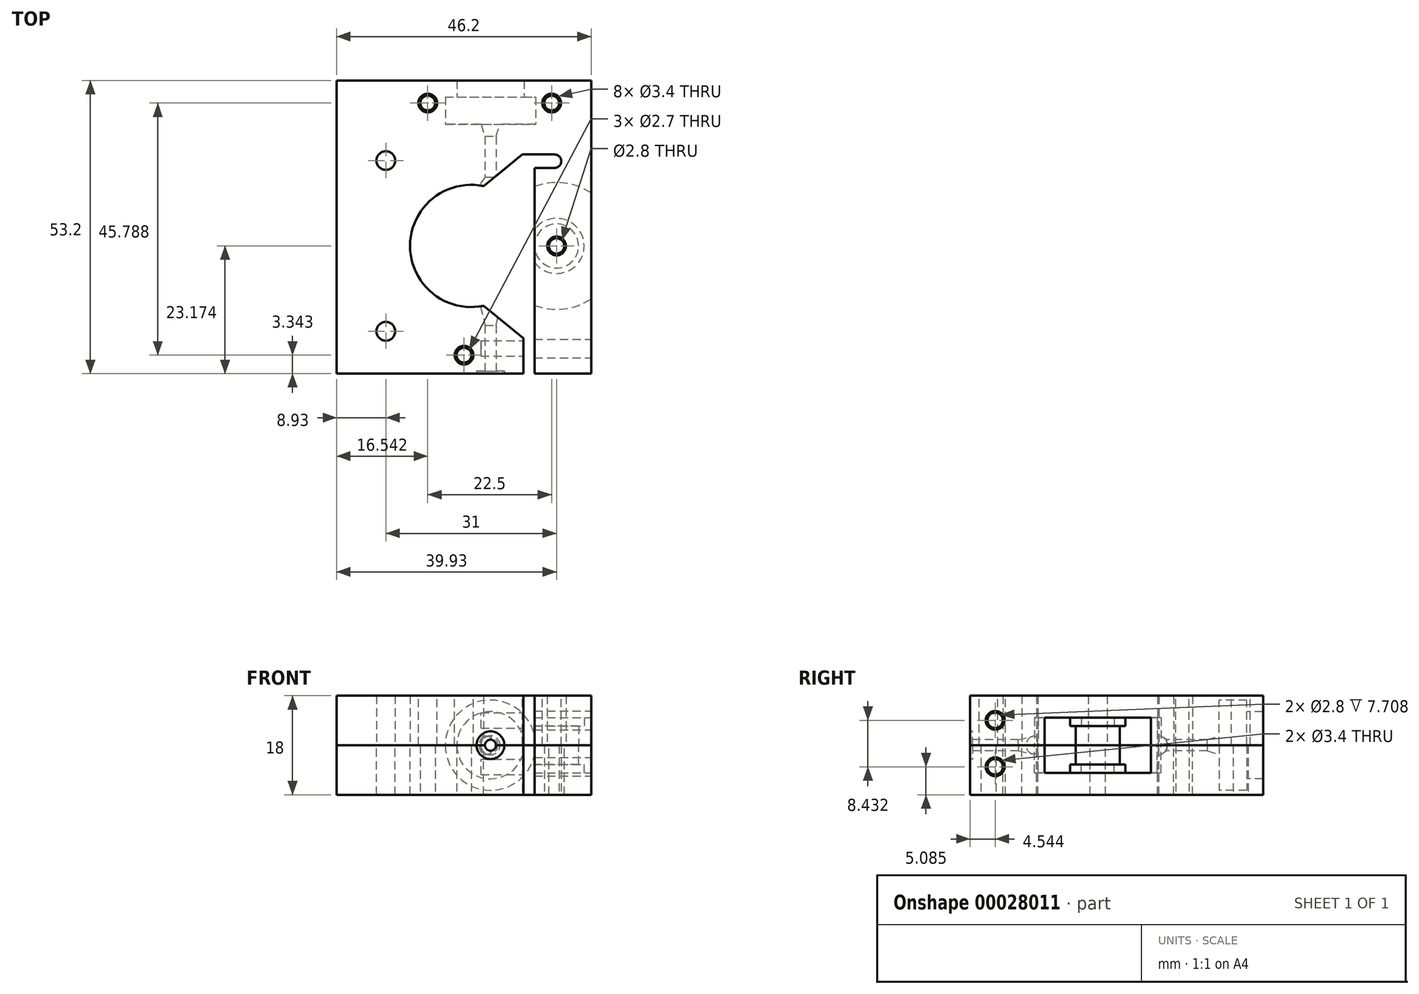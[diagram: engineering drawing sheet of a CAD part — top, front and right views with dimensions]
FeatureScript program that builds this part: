
annotation { "Feature Type Name" : "Feature", "Feature Type Description" : "" }
export const myFeature = defineFeature(function(context is Context, id is Id, definition is map)
    precondition{}
    {
        {
            var Q0;
            Q0=qCreatedBy(makeId("Top.planeOp"),FACE);
            var sketch = newSketch(context, id + "F0", { "sketchPlane" : qUnion([Q0])});
            skLineSegment(sketch, "E0", {"start": v(-24.43, 35.85) * mm, "end": v(-24.43, -17.36) * mm});
            skLineSegment(sketch, "E1", {"start": v(-24.43, -17.36) * mm, "end": v(-24.43, -17.36) * mm});
            skLineSegment(sketch, "E2", {"start": v(-24.43, -17.36) * mm, "end": v(-24.43, -17.35) * mm});
            skLineSegment(sketch, "E3", {"start": v(-24.43, -17.35) * mm, "end": v(9.48, -17.35) * mm});
            skLineSegment(sketch, "E4", {"start": v(9.48, -17.35) * mm, "end": v(9.48, 22.43) * mm});
            skLineSegment(sketch, "E5", {"start": v(9.48, 22.43) * mm, "end": v(15.14, 22.43) * mm});
            skLineSegment(sketch, "E6", {"start": v(15.14, 20) * mm, "end": v(11.48, 20) * mm});
            skLineSegment(sketch, "E7", {"start": v(11.48, 20) * mm, "end": v(11.48, -17.35) * mm});
            skLineSegment(sketch, "E8", {"start": v(11.48, -17.35) * mm, "end": v(21.77, -17.35) * mm});
            skLineSegment(sketch, "E9", {"start": v(21.77, -17.35) * mm, "end": v(21.77, 35.85) * mm});
            skLineSegment(sketch, "E10", {"start": v(21.77, 35.85) * mm, "end": v(-24.43, 35.85) * mm});
            skCircle(sketch, "E11", {"center": v(-7.89, 31.78) * mm, "radius": 1.35 * mm});
            skCircle(sketch, "E12", {"center": v(14.61, 31.78) * mm, "radius": 1.35 * mm});
            skCircle(sketch, "E13", {"center": v(-1.3, -14) * mm, "radius": 1.35 * mm});
            skArc(sketch, "E14", {"start": v(15.14, 20) * mm, "mid": v(16.35, 21.21) * mm, "end": v(15.14, 22.43) * mm});
            skCircle(sketch, "E15", {"center": v(-7.89, 31.78) * mm, "radius": 1.7 * mm});
            skCircle(sketch, "E16", {"center": v(14.61, 31.78) * mm, "radius": 1.7 * mm});
            skCircle(sketch, "E17", {"center": v(-1.3, -14) * mm, "radius": 1.7 * mm});
            skSolve(sketch);
        }
        {
            var Q0;
            Q0=makeQuery(id+"F0.imprint","IMPRINT",FACE,{"disambiguationData":[TD([[makeQuery(id+"F0.imprint","IMPRINT",EDGE,{"derivedFrom":sQuery(id+"F0.wireOp",EDGE,"E0")}),1.0]])]});
            var Q1;
            Q1=makeQuery(id+"F0.imprint","IMPRINT",FACE,{"disambiguationData":[TD([[makeQuery(id+"F0.imprint","IMPRINT",EDGE,{"derivedFrom":sQuery(id+"F0.wireOp",EDGE,"E11")}),-1.0]])]});
            var Q2;
            Q2=makeQuery(id+"F0.imprint","IMPRINT",FACE,{"disambiguationData":[TD([[makeQuery(id+"F0.imprint","IMPRINT",EDGE,{"derivedFrom":sQuery(id+"F0.wireOp",EDGE,"E12")}),-1.0]])]});
            var Q3;
            Q3=makeQuery(id+"F0.imprint","IMPRINT",FACE,{"disambiguationData":[TD([[makeQuery(id+"F0.imprint","IMPRINT",EDGE,{"derivedFrom":sQuery(id+"F0.wireOp",EDGE,"E13")}),-1.0]])]});
            extrude(context, id + "F1", {"entities" : qUnion([Q0, Q1, Q2, Q3]), "depth" : 9 * mm});
        }
        {
            var Q0;
            Q0=makeQuery(id+"F1.opExtrude","CAP_FACE",FACE,{"disambiguationData":[OSD([sQuery(id+"F0.wireOp",EDGE,"E0"),sQuery(id+"F0.wireOp",EDGE,"E1"),sQuery(id+"F0.wireOp",EDGE,"E2"),sQuery(id+"F0.wireOp",EDGE,"E3"),sQuery(id+"F0.wireOp",EDGE,"E4"),sQuery(id+"F0.wireOp",EDGE,"E5"),sQuery(id+"F0.wireOp",EDGE,"E6"),sQuery(id+"F0.wireOp",EDGE,"E7"),sQuery(id+"F0.wireOp",EDGE,"E8"),sQuery(id+"F0.wireOp",EDGE,"E9"),sQuery(id+"F0.wireOp",EDGE,"E10"),sQuery(id+"F0.wireOp",EDGE,"604cad85-587a-4b7d-8070-06f4cba85480"),sQuery(id+"F0.wireOp",EDGE,"6e5e38c1-5bff-4efe-a8c5-b84022f0a049"),sQuery(id+"F0.wireOp",EDGE,"b8144507-9dd7-4af4-87a3-7b649dd00ae6"),sQuery(id+"F0.wireOp",EDGE,"b9c2cb7c-5e58-4995-888e-a78f0403fbb5"),sQuery(id+"F0.wireOp",EDGE,"885990ab-7576-4c23-8475-595d2769e284"),sQuery(id+"F0.wireOp",EDGE,"E11"),sQuery(id+"F0.wireOp",EDGE,"E12"),sQuery(id+"F0.wireOp",EDGE,"E13"),sQuery(id+"F0.wireOp",EDGE,"E14")])],"isStart":false});
            var sketch = newSketch(context, id + "F2", { "sketchPlane" : qUnion([Q0])});
            skCircle(sketch, "E18", {"center": v(0, 5.82) * mm, "radius": 11.1 * mm});
            skCircle(sketch, "E19", {"center": v(-15.5, 21.32) * mm, "radius": 1.7 * mm});
            skCircle(sketch, "E20", {"center": v(-15.5, -9.68) * mm, "radius": 1.7 * mm});
            skSolve(sketch);
        }
        {
            var Q0;
            Q0=qSketchRegion(id+"F2",true);
            extrude(context, id + "F3", {"entities" : qUnion([Q0]), "operationType" : NewBodyOperationType.REMOVE, "endBound" : BoundingType.THROUGH_ALL, "oppositeDirection" : true, "depth" : 25 * mm});
        }
        {
            var Q0;
            Q0=makeQuery(id+"F1.opExtrude","CAP_FACE",FACE,{"disambiguationData":[OSD([sQuery(id+"F0.wireOp",EDGE,"E0"),sQuery(id+"F0.wireOp",EDGE,"E1"),sQuery(id+"F0.wireOp",EDGE,"E2"),sQuery(id+"F0.wireOp",EDGE,"E3"),sQuery(id+"F0.wireOp",EDGE,"E4"),sQuery(id+"F0.wireOp",EDGE,"E5"),sQuery(id+"F0.wireOp",EDGE,"E6"),sQuery(id+"F0.wireOp",EDGE,"E7"),sQuery(id+"F0.wireOp",EDGE,"E8"),sQuery(id+"F0.wireOp",EDGE,"E9"),sQuery(id+"F0.wireOp",EDGE,"E10"),sQuery(id+"F0.wireOp",EDGE,"604cad85-587a-4b7d-8070-06f4cba85480"),sQuery(id+"F0.wireOp",EDGE,"6e5e38c1-5bff-4efe-a8c5-b84022f0a049"),sQuery(id+"F0.wireOp",EDGE,"E11"),sQuery(id+"F0.wireOp",EDGE,"E12"),sQuery(id+"F0.wireOp",EDGE,"E13"),sQuery(id+"F0.wireOp",EDGE,"E14")])],"isStart":false});
            var sketch = newSketch(context, id + "F4", { "sketchPlane" : qUnion([Q0])});
            skCircle(sketch, "E21", {"center": v(15.5, 5.82) * mm, "radius": 11.5 * mm});
            skCircle(sketch, "E22", {"center": v(15.5, 5.82) * mm, "radius": 5 * mm});
            skCircle(sketch, "E23", {"center": v(15.5, 5.82) * mm, "radius": 4 * mm});
            skLineSegment(sketch, "E24", {"start": v(0, 5.82) * mm, "end": v(31, 5.82) * mm, "construction": true});
            skCircle(sketch, "E25", {"center": v(15.5, 5.82) * mm, "radius": 1.4 * mm});
            skCircle(sketch, "E26", {"center": v(15.5, 5.82) * mm, "radius": 1.7 * mm});
            skSolve(sketch);
        }
        {
            var Q0;
            Q0=makeQuery(id+"F4.imprint","IMPRINT",FACE,{"disambiguationData":[TD([[makeQuery(id+"F4.imprint","IMPRINT",EDGE,{"derivedFrom":sQuery(id+"F4.wireOp",EDGE,"E22")}),-1.0]])]});
            extrude(context, id + "F5", {"entities" : qUnion([Q0]), "operationType" : NewBodyOperationType.REMOVE, "oppositeDirection" : true, "depth" : 5 * mm});
        }
        {
            var Q0;
            Q0=makeQuery(id+"F4.imprint","IMPRINT",FACE,{"disambiguationData":[TD([[makeQuery(id+"F4.imprint","IMPRINT",EDGE,{"derivedFrom":sQuery(id+"F4.wireOp",EDGE,"E22")}),1.0]])]});
            var Q1;
            Q1=makeQuery(id+"F4.imprint","IMPRINT",FACE,{"disambiguationData":[TD([[makeQuery(id+"F4.imprint","IMPRINT",EDGE,{"derivedFrom":sQuery(id+"F4.wireOp",EDGE,"E23")}),-1.0]])]});
            extrude(context, id + "F6", {"entities" : qUnion([Q0, Q1]), "operationType" : NewBodyOperationType.REMOVE, "oppositeDirection" : true, "depth" : 3.5 * mm});
        }
        {
            var Q0;
            {var subQ0=sQuery(id+"F0.wireOp",EDGE,"E0");var subQ1=sQuery(id+"F0.wireOp",EDGE,"E1");var subQ2=sQuery(id+"F0.wireOp",EDGE,"E2");var subQ3=sQuery(id+"F0.wireOp",EDGE,"E3");var subQ4=sQuery(id+"F0.wireOp",EDGE,"E4");var subQ5=sQuery(id+"F0.wireOp",EDGE,"E5");var subQ6=sQuery(id+"F0.wireOp",EDGE,"E6");var subQ7=sQuery(id+"F0.wireOp",EDGE,"E7");var subQ8=sQuery(id+"F0.wireOp",EDGE,"E9");var subQ9=sQuery(id+"F0.wireOp",EDGE,"E10");var subQ10=sQuery(id+"F0.wireOp",EDGE,"604cad85-587a-4b7d-8070-06f4cba85480");var subQ11=sQuery(id+"F0.wireOp",EDGE,"6e5e38c1-5bff-4efe-a8c5-b84022f0a049");var subQ12=sQuery(id+"F0.wireOp",EDGE,"E11");var subQ13=sQuery(id+"F0.wireOp",EDGE,"E12");var subQ14=sQuery(id+"F0.wireOp",EDGE,"E13");var subQ15=sQuery(id+"F0.wireOp",EDGE,"E14");Q0=makeQuery(id+"F5.boolean.opBoolean","SPLIT",FACE,{"disambiguationData":[TD([makeQuery(id+"F1.opExtrude","SWEPT_FACE",FACE,{"disambiguationData":[OSD([subQ0])]})])],"derivedFrom":makeQuery(id+"F1.opExtrude","CAP_FACE",FACE,{"disambiguationData":[OSD([subQ0,subQ1,subQ2,subQ3,subQ4,subQ5,subQ6,subQ7,sQuery(id+"F0.wireOp",EDGE,"E8"),subQ8,subQ9,subQ10,subQ11,subQ12,subQ13,subQ14,subQ15])],"isStart":false})});}
            var sketch = newSketch(context, id + "F7", { "sketchPlane" : qUnion([Q0])});
            skLineSegment(sketch, "E27", {"start": v(3.5, 14.7) * mm, "end": v(3.5, 37.09) * mm});
            skLineSegment(sketch, "E28", {"start": v(0, 5.82) * mm, "end": v(31.4, 5.82) * mm, "construction": true});
            skLineSegment(sketch, "E29.0.MirrorCS", {"start": v(0.98, -16.94) * mm, "end": v(2.5, -16.94) * mm});
            skLineSegment(sketch, "E29.1.MirrorCS", {"start": v(3.5, -3.06) * mm, "end": v(3.5, -25.44) * mm});
            skLineSegment(sketch, "E29.2.MirrorCS", {"start": v(0.98, -25.44) * mm, "end": v(0.98, -16.94) * mm});
            skLineSegment(sketch, "E29.3.MirrorCS", {"start": v(1.31, -3.53) * mm, "end": v(3.5, -3.06) * mm});
            skLineSegment(sketch, "E29.4.MirrorCS", {"start": v(2.5, -8.56) * mm, "end": v(1.31, -3.53) * mm});
            skLineSegment(sketch, "E29.5.MirrorCS", {"start": v(2.5, -16.94) * mm, "end": v(2.5, -8.56) * mm});
            skLineSegment(sketch, "E29.6.MirrorCS", {"start": v(3.5, -25.44) * mm, "end": v(0.98, -25.44) * mm});
            skLineSegment(sketch, "E30", {"start": v(-2.6, 37.09) * mm, "end": v(-2.6, 32.89) * mm});
            skLineSegment(sketch, "E31", {"start": v(-2.6, 32.89) * mm, "end": v(-4.7, 32.89) * mm});
            skLineSegment(sketch, "E32", {"start": v(-4.7, 32.89) * mm, "end": v(-4.7, 27.89) * mm});
            skLineSegment(sketch, "E33", {"start": v(-4.7, 27.89) * mm, "end": v(1.77, 27.89) * mm});
            skLineSegment(sketch, "E34", {"start": v(1.77, 27.89) * mm, "end": v(2.5, 25.73) * mm});
            skLineSegment(sketch, "E35", {"start": v(2.5, 25.73) * mm, "end": v(2.5, 18.34) * mm});
            skLineSegment(sketch, "E36", {"start": v(-2.6, 37.09) * mm, "end": v(3.5, 37.09) * mm});
            skLineSegment(sketch, "E37", {"start": v(2.5, 18.34) * mm, "end": v(0, 14.7) * mm});
            skLineSegment(sketch, "E38", {"start": v(0, 14.7) * mm, "end": v(3.5, 14.7) * mm});
            skSolve(sketch);
        }
        {
            var Q0;
            Q0=qSketchRegion(id+"F7",true);
            var Q1;
            Q1=sQuery(id+"F7.wireOp",EDGE,"E27");
            revolve(context, id + "F8", {"entities" : qUnion([Q0]), "axis" : qUnion([Q1]), "revolveType" : RevolveType.FULL});
        }
        {
            var Q0;
            Q0=makeQuery(id+"F8.opRevolve","SWEPT_BODY",BODY,{"disambiguationData":[OSD([sQuery(id+"F7.wireOp",EDGE,"0e4a01cc-4869-4b9d-8ca2-1c94110d196d"),sQuery(id+"F7.wireOp",EDGE,"4d913e13-2244-4a79-84d2-82f6c5de00b3"),sQuery(id+"F7.wireOp",EDGE,"1203443b-fa58-4cec-9fe4-144960d3b7c2"),sQuery(id+"F7.wireOp",EDGE,"f73e5a92-9274-40af-91db-ab5fa52ec61f"),sQuery(id+"F7.wireOp",EDGE,"4cc6588a-36a6-4115-9f4e-735cf5f17870"),sQuery(id+"F7.wireOp",EDGE,"E27"),sQuery(id+"F7.wireOp",EDGE,"0bbee7b9-97e0-41c3-ac0e-625151f8027d")])]});
            var Q1;
            Q1=makeQuery(id+"F1.opExtrude","SWEPT_BODY",BODY,{"disambiguationData":[OSD([sQuery(id+"F0.wireOp",EDGE,"E0"),sQuery(id+"F0.wireOp",EDGE,"E1"),sQuery(id+"F0.wireOp",EDGE,"E2"),sQuery(id+"F0.wireOp",EDGE,"E3"),sQuery(id+"F0.wireOp",EDGE,"E4"),sQuery(id+"F0.wireOp",EDGE,"E5"),sQuery(id+"F0.wireOp",EDGE,"E6"),sQuery(id+"F0.wireOp",EDGE,"E7"),sQuery(id+"F0.wireOp",EDGE,"E8"),sQuery(id+"F0.wireOp",EDGE,"E9"),sQuery(id+"F0.wireOp",EDGE,"E10"),sQuery(id+"F0.wireOp",EDGE,"604cad85-587a-4b7d-8070-06f4cba85480"),sQuery(id+"F0.wireOp",EDGE,"6e5e38c1-5bff-4efe-a8c5-b84022f0a049"),sQuery(id+"F0.wireOp",EDGE,"E11"),sQuery(id+"F0.wireOp",EDGE,"E12"),sQuery(id+"F0.wireOp",EDGE,"E13"),sQuery(id+"F0.wireOp",EDGE,"E14")])]});
            booleanBodies(context, id + "F9", {"operationType" : BooleanOperationType.SUBTRACTION, "tools" : qUnion([Q0]), "targets" : qUnion([Q1]), "keepTools" : true});
        }
        {
            var Q0;
            Q0=makeQuery(id+"F8.opRevolve","SWEPT_BODY",BODY,{"disambiguationData":[OSD([sQuery(id+"F7.wireOp",EDGE,"E29.0.MirrorCS"),sQuery(id+"F7.wireOp",EDGE,"E29.1.MirrorCS"),sQuery(id+"F7.wireOp",EDGE,"E29.2.MirrorCS"),sQuery(id+"F7.wireOp",EDGE,"E29.3.MirrorCS"),sQuery(id+"F7.wireOp",EDGE,"E29.4.MirrorCS"),sQuery(id+"F7.wireOp",EDGE,"E29.5.MirrorCS"),sQuery(id+"F7.wireOp",EDGE,"E29.6.MirrorCS")])]});
            var Q1;
            Q1=makeQuery(id+"F1.opExtrude","SWEPT_BODY",BODY,{"disambiguationData":[OSD([sQuery(id+"F0.wireOp",EDGE,"E0"),sQuery(id+"F0.wireOp",EDGE,"E1"),sQuery(id+"F0.wireOp",EDGE,"E2"),sQuery(id+"F0.wireOp",EDGE,"E3"),sQuery(id+"F0.wireOp",EDGE,"E4"),sQuery(id+"F0.wireOp",EDGE,"E5"),sQuery(id+"F0.wireOp",EDGE,"E6"),sQuery(id+"F0.wireOp",EDGE,"E7"),sQuery(id+"F0.wireOp",EDGE,"E8"),sQuery(id+"F0.wireOp",EDGE,"E9"),sQuery(id+"F0.wireOp",EDGE,"E10"),sQuery(id+"F0.wireOp",EDGE,"604cad85-587a-4b7d-8070-06f4cba85480"),sQuery(id+"F0.wireOp",EDGE,"6e5e38c1-5bff-4efe-a8c5-b84022f0a049"),sQuery(id+"F0.wireOp",EDGE,"E11"),sQuery(id+"F0.wireOp",EDGE,"E12"),sQuery(id+"F0.wireOp",EDGE,"E13"),sQuery(id+"F0.wireOp",EDGE,"E14")])]});
            booleanBodies(context, id + "F10", {"operationType" : BooleanOperationType.SUBTRACTION, "tools" : qUnion([Q0]), "targets" : qUnion([Q1]), "keepTools" : true});
        }
        {
            var Q0;
            Q0=qSketchRegion(id+"F0",true);
            extrude(context, id + "F11", {"entities" : qUnion([Q0]), "oppositeDirection" : true, "depth" : 9 * mm});
        }
        {
            var Q0;
            Q0=makeQuery(id+"F11.opExtrude","SWEPT_BODY",BODY,{"disambiguationData":[OSD([sQuery(id+"F0.wireOp",EDGE,"E0"),sQuery(id+"F0.wireOp",EDGE,"E3"),sQuery(id+"F0.wireOp",EDGE,"E4"),sQuery(id+"F0.wireOp",EDGE,"E5"),sQuery(id+"F0.wireOp",EDGE,"E6"),sQuery(id+"F0.wireOp",EDGE,"E7"),sQuery(id+"F0.wireOp",EDGE,"E8"),sQuery(id+"F0.wireOp",EDGE,"E9"),sQuery(id+"F0.wireOp",EDGE,"E10"),sQuery(id+"F0.wireOp",EDGE,"E11"),sQuery(id+"F0.wireOp",EDGE,"E12"),sQuery(id+"F0.wireOp",EDGE,"E13"),sQuery(id+"F0.wireOp",EDGE,"E14")])]});
            transform(context, id + "F12", {"entities" : qUnion([Q0]), "transformType" : TransformType.TRANSLATION_3D, "dx" : 0 * mm, "dy" : 0 * mm, "dz" : 18 * mm, "makeCopy" : false});
        }
        {
            var Q0;
            Q0=qSketchRegion(id+"F2",true);
            extrude(context, id + "F13", {"entities" : qUnion([Q0]), "operationType" : NewBodyOperationType.REMOVE, "endBound" : BoundingType.THROUGH_ALL, "depth" : 25 * mm});
        }
        {
            var Q0;
            {var subQ3=sQuery(id+"F4.wireOp",EDGE,"E21");var subQ7=makeQuery(id+"F1.opExtrude","CAP_EDGE",EDGE,{"disambiguationData":[OSD([sQuery(id+"F0.wireOp",EDGE,"E9")])],"isStart":false});var subQ9=makeQuery(id+"F4.imprint","INTERSECT",VERTEX,{"disambiguationData":[OD(0.0)],"derivedFrom":[subQ7,subQ3]});Q0=makeQuery(id+"F4.imprint","IMPRINT",FACE,{"disambiguationData":[TD([[makeQuery(id+"F4.imprint","IMPRINT",EDGE,{"disambiguationData":[TD([[subQ9,-1.0]])],"derivedFrom":subQ3}),1.0]])]});}
            extrude(context, id + "F14", {"entities" : qUnion([Q0]), "operationType" : NewBodyOperationType.REMOVE, "depth" : 5 * mm});
        }
        {
            var Q0;
            Q0=makeQuery(id+"F4.imprint","IMPRINT",FACE,{"disambiguationData":[TD([[makeQuery(id+"F4.imprint","IMPRINT",EDGE,{"derivedFrom":sQuery(id+"F4.wireOp",EDGE,"E23")}),-1.0]])]});
            extrude(context, id + "F15", {"entities" : qUnion([Q0]), "operationType" : NewBodyOperationType.REMOVE, "depth" : 3.5 * mm});
        }
        {
            var Q0;
            Q0=makeQuery(id+"F8.opRevolve","SWEPT_BODY",BODY,{"disambiguationData":[OSD([sQuery(id+"F7.wireOp",EDGE,"0e4a01cc-4869-4b9d-8ca2-1c94110d196d"),sQuery(id+"F7.wireOp",EDGE,"4d913e13-2244-4a79-84d2-82f6c5de00b3"),sQuery(id+"F7.wireOp",EDGE,"1203443b-fa58-4cec-9fe4-144960d3b7c2"),sQuery(id+"F7.wireOp",EDGE,"f73e5a92-9274-40af-91db-ab5fa52ec61f"),sQuery(id+"F7.wireOp",EDGE,"4cc6588a-36a6-4115-9f4e-735cf5f17870"),sQuery(id+"F7.wireOp",EDGE,"E27"),sQuery(id+"F7.wireOp",EDGE,"0bbee7b9-97e0-41c3-ac0e-625151f8027d")])]});
            var Q1;
            Q1=makeQuery(id+"F11.opExtrude","SWEPT_BODY",BODY,{"disambiguationData":[OSD([sQuery(id+"F0.wireOp",EDGE,"E0"),sQuery(id+"F0.wireOp",EDGE,"E3"),sQuery(id+"F0.wireOp",EDGE,"E4"),sQuery(id+"F0.wireOp",EDGE,"E5"),sQuery(id+"F0.wireOp",EDGE,"E6"),sQuery(id+"F0.wireOp",EDGE,"E7"),sQuery(id+"F0.wireOp",EDGE,"E8"),sQuery(id+"F0.wireOp",EDGE,"E9"),sQuery(id+"F0.wireOp",EDGE,"E10"),sQuery(id+"F0.wireOp",EDGE,"E11"),sQuery(id+"F0.wireOp",EDGE,"E12"),sQuery(id+"F0.wireOp",EDGE,"E13"),sQuery(id+"F0.wireOp",EDGE,"E14")])]});
            booleanBodies(context, id + "F16", {"operationType" : BooleanOperationType.SUBTRACTION, "tools" : qUnion([Q0]), "targets" : qUnion([Q1])});
        }
        {
            var Q0;
            Q0=makeQuery(id+"F8.opRevolve","SWEPT_BODY",BODY,{"disambiguationData":[OSD([sQuery(id+"F7.wireOp",EDGE,"E29.0.MirrorCS"),sQuery(id+"F7.wireOp",EDGE,"E29.1.MirrorCS"),sQuery(id+"F7.wireOp",EDGE,"E29.2.MirrorCS"),sQuery(id+"F7.wireOp",EDGE,"E29.3.MirrorCS"),sQuery(id+"F7.wireOp",EDGE,"E29.4.MirrorCS"),sQuery(id+"F7.wireOp",EDGE,"E29.5.MirrorCS"),sQuery(id+"F7.wireOp",EDGE,"E29.6.MirrorCS")])]});
            var Q1;
            Q1=makeQuery(id+"F11.opExtrude","SWEPT_BODY",BODY,{"disambiguationData":[OSD([sQuery(id+"F0.wireOp",EDGE,"E0"),sQuery(id+"F0.wireOp",EDGE,"E3"),sQuery(id+"F0.wireOp",EDGE,"E4"),sQuery(id+"F0.wireOp",EDGE,"E5"),sQuery(id+"F0.wireOp",EDGE,"E6"),sQuery(id+"F0.wireOp",EDGE,"E7"),sQuery(id+"F0.wireOp",EDGE,"E8"),sQuery(id+"F0.wireOp",EDGE,"E9"),sQuery(id+"F0.wireOp",EDGE,"E10"),sQuery(id+"F0.wireOp",EDGE,"E11"),sQuery(id+"F0.wireOp",EDGE,"E12"),sQuery(id+"F0.wireOp",EDGE,"E13"),sQuery(id+"F0.wireOp",EDGE,"E14")])]});
            booleanBodies(context, id + "F17", {"operationType" : BooleanOperationType.SUBTRACTION, "tools" : qUnion([Q0]), "targets" : qUnion([Q1])});
        }
        {
            var Q0;
            Q0=makeQuery(id+"F11.opExtrude","SWEPT_FACE",FACE,{"disambiguationData":[OSD([sQuery(id+"F0.wireOp",EDGE,"E9")])]});
            var sketch = newSketch(context, id + "F18", { "sketchPlane" : qUnion([Q0])});
            skCircle(sketch, "E39", {"center": v(-12.8, 13.52) * mm, "radius": 1.7 * mm});
            skCircle(sketch, "E40", {"center": v(-12.8, 13.52) * mm, "radius": 1.4 * mm});
            skCircle(sketch, "E41", {"center": v(-12.8, 5.09) * mm, "radius": 1.7 * mm});
            skCircle(sketch, "E42", {"center": v(-12.8, 5.09) * mm, "radius": 1.4 * mm});
            skSolve(sketch);
        }
        {
            var Q0;
            Q0=makeQuery(id+"F18.imprint","IMPRINT",FACE,{"disambiguationData":[TD([[makeQuery(id+"F18.imprint","IMPRINT",EDGE,{"derivedFrom":sQuery(id+"F18.wireOp",EDGE,"E40")}),1.0]])]});
            extrude(context, id + "F19", {"entities" : qUnion([Q0]), "operationType" : NewBodyOperationType.REMOVE, "oppositeDirection" : true, "depth" : 20 * mm});
        }
        {
            var Q0;
            Q0=makeQuery(id+"F18.imprint","IMPRINT",FACE,{"disambiguationData":[TD([[makeQuery(id+"F18.imprint","IMPRINT",EDGE,{"derivedFrom":sQuery(id+"F18.wireOp",EDGE,"E39")}),1.0]])]});
            extrude(context, id + "F20", {"entities" : qUnion([Q0]), "operationType" : NewBodyOperationType.REMOVE, "oppositeDirection" : true, "depth" : 11 * mm});
        }
        {
            var Q0;
            Q0=makeQuery(id+"F18.imprint","IMPRINT",FACE,{"disambiguationData":[TD([[makeQuery(id+"F18.imprint","IMPRINT",EDGE,{"derivedFrom":sQuery(id+"F18.wireOp",EDGE,"E42")}),1.0]])]});
            extrude(context, id + "F21", {"entities" : qUnion([Q0]), "operationType" : NewBodyOperationType.REMOVE, "oppositeDirection" : true, "depth" : 20 * mm});
        }
        {
            var Q0;
            Q0=makeQuery(id+"F18.imprint","IMPRINT",FACE,{"disambiguationData":[TD([[makeQuery(id+"F18.imprint","IMPRINT",EDGE,{"derivedFrom":sQuery(id+"F18.wireOp",EDGE,"E41")}),1.0]])]});
            extrude(context, id + "F22", {"entities" : qUnion([Q0]), "operationType" : NewBodyOperationType.REMOVE, "oppositeDirection" : true, "depth" : 11 * mm});
        }
        {
            var Q0;
            Q0=makeQuery(id+"F4.imprint","IMPRINT",FACE,{"disambiguationData":[TD([[makeQuery(id+"F4.imprint","IMPRINT",EDGE,{"derivedFrom":sQuery(id+"F4.wireOp",EDGE,"E25")}),1.0]])]});
            extrude(context, id + "F23", {"entities" : qUnion([Q0]), "operationType" : NewBodyOperationType.REMOVE, "endBound" : BoundingType.THROUGH_ALL, "oppositeDirection" : true, "depth" : 25 * mm});
        }
        {
            var Q0;
            Q0=makeQuery(id+"F4.imprint","IMPRINT",FACE,{"disambiguationData":[TD([[makeQuery(id+"F4.imprint","IMPRINT",EDGE,{"derivedFrom":sQuery(id+"F4.wireOp",EDGE,"E25")}),1.0]])]});
            var Q1;
            Q1=makeQuery(id+"F4.imprint","IMPRINT",FACE,{"disambiguationData":[TD([[makeQuery(id+"F4.imprint","IMPRINT",EDGE,{"derivedFrom":sQuery(id+"F4.wireOp",EDGE,"E25")}),-1.0]])]});
            extrude(context, id + "F24", {"entities" : qUnion([Q0, Q1]), "operationType" : NewBodyOperationType.REMOVE, "endBound" : BoundingType.THROUGH_ALL, "depth" : 25 * mm});
        }
        {
            var Q0;
            Q0=makeQuery(id+"F3.boolean.opBoolean","INTERSECT",EDGE,{"disambiguationData":[OD(0.0)],"derivedFrom":[makeQuery(id+"F1.opExtrude","SWEPT_FACE",FACE,{"disambiguationData":[OSD([sQuery(id+"F0.wireOp",EDGE,"E4")])]}),makeQuery(id+"F3.opExtrude","SWEPT_FACE",FACE,{"disambiguationData":[OSD([sQuery(id+"F2.wireOp",EDGE,"E18")])]})]});
            var Q1;
            Q1=makeQuery(id+"F3.boolean.opBoolean","INTERSECT",EDGE,{"disambiguationData":[OD(1.0)],"derivedFrom":[makeQuery(id+"F1.opExtrude","SWEPT_FACE",FACE,{"disambiguationData":[OSD([sQuery(id+"F0.wireOp",EDGE,"E4")])]}),makeQuery(id+"F3.opExtrude","SWEPT_FACE",FACE,{"disambiguationData":[OSD([sQuery(id+"F2.wireOp",EDGE,"E18")])]})]});
            var Q2;
            Q2=makeQuery(id+"F13.boolean.opBoolean","INTERSECT",EDGE,{"disambiguationData":[OD(1.0)],"derivedFrom":[makeQuery(id+"F11.opExtrude","SWEPT_FACE",FACE,{"disambiguationData":[OSD([sQuery(id+"F0.wireOp",EDGE,"E4")])]}),makeQuery(id+"F13.opExtrude","SWEPT_FACE",FACE,{"disambiguationData":[OSD([sQuery(id+"F2.wireOp",EDGE,"E18")])]})]});
            var Q3;
            Q3=makeQuery(id+"F13.boolean.opBoolean","INTERSECT",EDGE,{"disambiguationData":[OD(0.0)],"derivedFrom":[makeQuery(id+"F11.opExtrude","SWEPT_FACE",FACE,{"disambiguationData":[OSD([sQuery(id+"F0.wireOp",EDGE,"E4")])]}),makeQuery(id+"F13.opExtrude","SWEPT_FACE",FACE,{"disambiguationData":[OSD([sQuery(id+"F2.wireOp",EDGE,"E18")])]})]});
            chamfer(context, id + "F25", {"entities" : qUnion([Q0, Q1, Q2, Q3]), "width" : 6 * mm, "tangentPropagation" : true});
        }
    });
